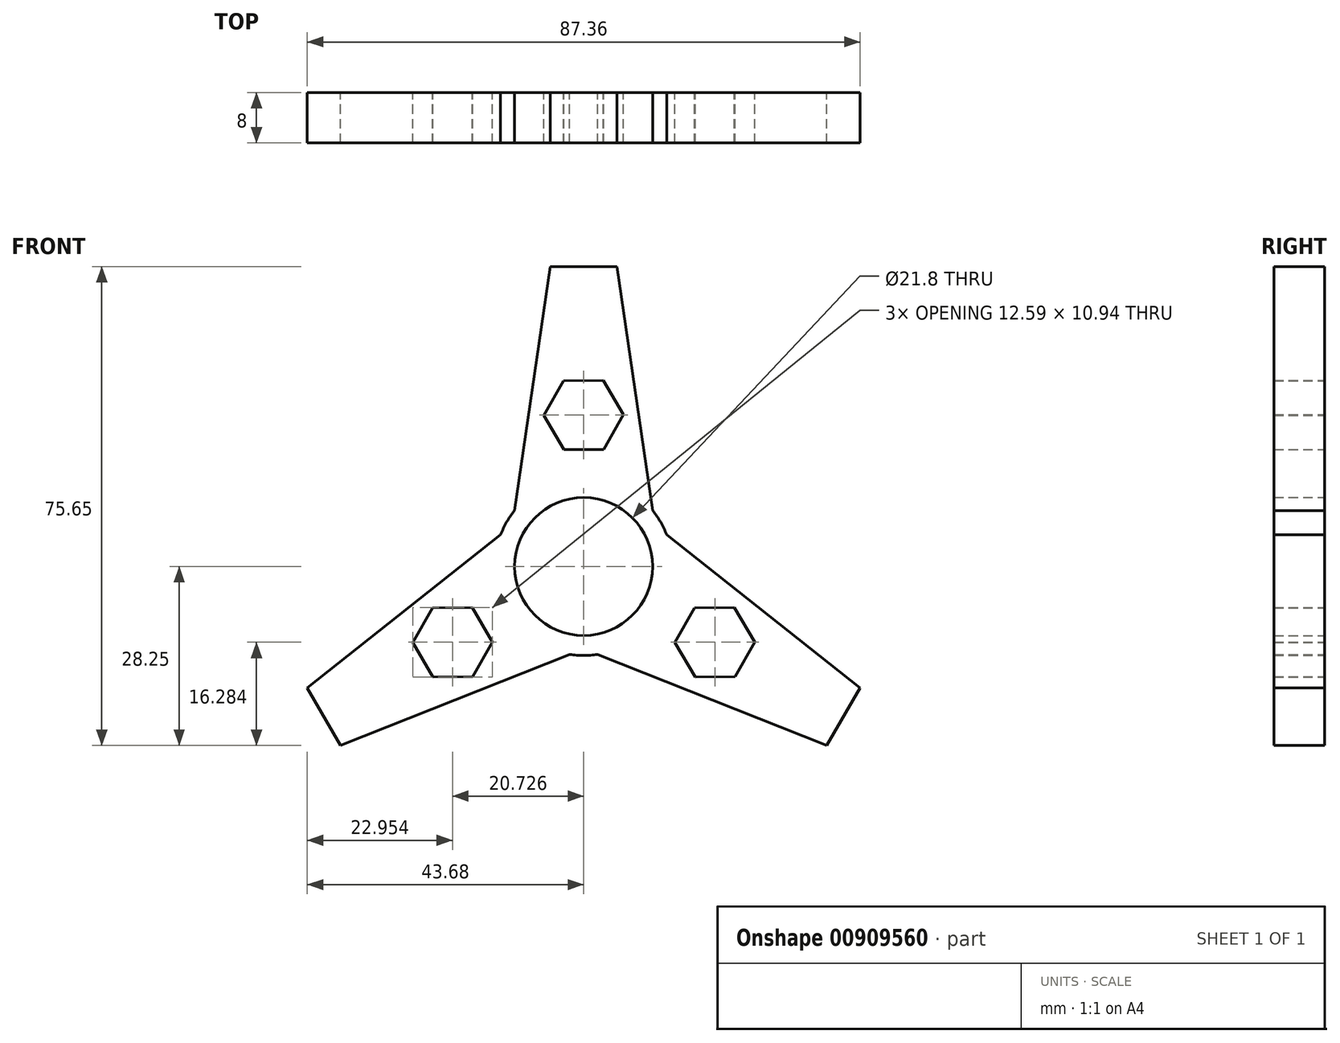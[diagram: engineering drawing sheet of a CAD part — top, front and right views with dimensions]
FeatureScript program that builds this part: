
annotation { "Feature Type Name" : "Feature", "Feature Type Description" : "" }
export const myFeature = defineFeature(function(context is Context, id is Id, definition is map)
    precondition{}
    {
        {
            var Q0;
            Q0=qCreatedBy(makeId("Front.planeOp"),FACE);
            var sketch = newSketch(context, id + "F0", { "sketchPlane" : qUnion([Q0])});
            skCircle(sketch, "E0", {"center": v(0, 0) * mm, "radius": 10.9 * mm});
            skCircle(sketch, "E1", {"center": v(0, 0) * mm, "radius": 14.05 * mm});
            skLineSegment(sketch, "E2", {"start": v(-10.92, 8.84) * mm, "end": v(-5.26, 47.4) * mm});
            skLineSegment(sketch, "E3", {"start": v(-5.26, 47.4) * mm, "end": v(0, 47.4) * mm});
            skLineSegment(sketch, "E4.MirrorCS", {"start": v(10.92, 8.84) * mm, "end": v(5.26, 47.4) * mm});
            skLineSegment(sketch, "E5.MirrorCS", {"start": v(5.26, 47.4) * mm, "end": v(0, 47.4) * mm});
            skLineSegment(sketch, "E6.1.0", {"start": v(-2.2, -13.88) * mm, "end": v(-38.42, -28.25) * mm});
            skLineSegment(sketch, "E6.1.1", {"start": v(-13.12, 5.03) * mm, "end": v(-43.68, -19.14) * mm});
            skLineSegment(sketch, "E6.1.2", {"start": v(-43.68, -19.14) * mm, "end": v(-41.05, -23.7) * mm});
            skLineSegment(sketch, "E6.1.3", {"start": v(-38.42, -28.25) * mm, "end": v(-41.05, -23.7) * mm});
            skLineSegment(sketch, "E6.2.0", {"start": v(13.12, 5.03) * mm, "end": v(43.68, -19.14) * mm});
            skLineSegment(sketch, "E6.2.1", {"start": v(2.2, -13.88) * mm, "end": v(38.42, -28.25) * mm});
            skLineSegment(sketch, "E6.2.2", {"start": v(38.42, -28.25) * mm, "end": v(41.05, -23.7) * mm});
            skLineSegment(sketch, "E6.2.3", {"start": v(43.68, -19.14) * mm, "end": v(41.05, -23.7) * mm});
            skCircle(sketch, "E7.cCircle", {"center": v(0, 23.93) * mm, "radius": 5.45 * mm, "construction": true});
            skLineSegment(sketch, "E7.0", {"start": v(-3.1, 18.46) * mm, "end": v(-6.3, 23.89) * mm});
            skLineSegment(sketch, "E7.1", {"start": v(-6.3, 23.89) * mm, "end": v(-3.18, 29.36) * mm});
            skLineSegment(sketch, "E7.2", {"start": v(-3.18, 29.36) * mm, "end": v(3.1, 29.4) * mm});
            skLineSegment(sketch, "E7.3", {"start": v(3.1, 29.4) * mm, "end": v(6.3, 23.98) * mm});
            skLineSegment(sketch, "E7.4", {"start": v(6.3, 23.98) * mm, "end": v(3.18, 18.5) * mm});
            skLineSegment(sketch, "E7.5", {"start": v(3.18, 18.5) * mm, "end": v(-3.1, 18.46) * mm});
            skPoint(sketch, "E7.0.midPoint", {"position": v(-4.7, 21.18) * mm});
            skLineSegment(sketch, "E8.1.0", {"start": v(-23.84, -17.44) * mm, "end": v(-27.02, -12) * mm});
            skLineSegment(sketch, "E8.1.1", {"start": v(-27.02, -12) * mm, "end": v(-23.9, -6.54) * mm});
            skLineSegment(sketch, "E8.1.2", {"start": v(-23.9, -6.54) * mm, "end": v(-17.62, -6.5) * mm});
            skLineSegment(sketch, "E8.1.3", {"start": v(-17.62, -6.5) * mm, "end": v(-14.43, -11.92) * mm});
            skCircle(sketch, "E8.1.4", {"center": v(-20.73, -11.97) * mm, "radius": 5.45 * mm, "construction": true});
            skLineSegment(sketch, "E8.1.5", {"start": v(-17.54, -17.4) * mm, "end": v(-23.84, -17.44) * mm});
            skLineSegment(sketch, "E8.1.6", {"start": v(-14.43, -11.92) * mm, "end": v(-17.54, -17.4) * mm});
            skLineSegment(sketch, "E8.2.0", {"start": v(27.02, -11.92) * mm, "end": v(23.9, -17.4) * mm});
            skLineSegment(sketch, "E8.2.1", {"start": v(23.9, -17.4) * mm, "end": v(17.62, -17.44) * mm});
            skLineSegment(sketch, "E8.2.2", {"start": v(17.62, -17.44) * mm, "end": v(14.43, -12) * mm});
            skLineSegment(sketch, "E8.2.3", {"start": v(14.43, -12) * mm, "end": v(17.54, -6.54) * mm});
            skCircle(sketch, "E8.2.4", {"center": v(20.73, -11.97) * mm, "radius": 5.45 * mm, "construction": true});
            skLineSegment(sketch, "E8.2.5", {"start": v(23.84, -6.5) * mm, "end": v(27.02, -11.92) * mm});
            skLineSegment(sketch, "E8.2.6", {"start": v(17.54, -6.54) * mm, "end": v(23.84, -6.5) * mm});
            skSolve(sketch);
        }
        {
            var Q0;
            {var subQ1=sQuery(id+"F0.wireOp",EDGE,"E6.2.0");Q0=makeQuery(id+"F0.imprint","IMPRINT",FACE,{"disambiguationData":[TD([[makeQuery(id+"F0.imprint","IMPRINT",EDGE,{"derivedFrom":subQ1}),-1.0]])]});}
            var Q1;
            {var subQ0=sQuery(id+"F0.wireOp",EDGE,"E2");Q1=makeQuery(id+"F0.imprint","IMPRINT",FACE,{"disambiguationData":[TD([[makeQuery(id+"F0.imprint","IMPRINT",EDGE,{"derivedFrom":subQ0}),-1.0]])]});}
            var Q2;
            {var subQ0=sQuery(id+"F0.wireOp",EDGE,"E6.1.0");Q2=makeQuery(id+"F0.imprint","IMPRINT",FACE,{"disambiguationData":[TD([[makeQuery(id+"F0.imprint","IMPRINT",EDGE,{"derivedFrom":subQ0}),-1.0]])]});}
            var Q3;
            Q3=makeQuery(id+"F0.imprint","IMPRINT",FACE,{"disambiguationData":[TD([[makeQuery(id+"F0.imprint","IMPRINT",EDGE,{"derivedFrom":sQuery(id+"F0.wireOp",EDGE,"E0")}),-1.0]])]});
            extrude(context, id + "F1", {"entities" : qUnion([Q0, Q1, Q2, Q3]), "depth" : 8 * mm, "offsetDistance" : 25 * mm});
        }
    });
